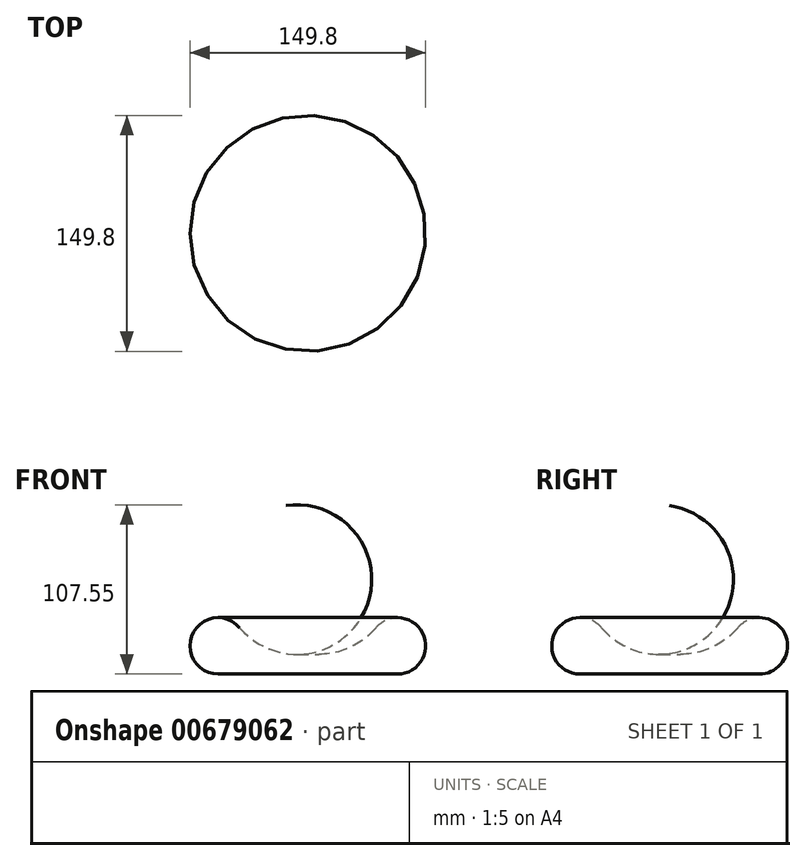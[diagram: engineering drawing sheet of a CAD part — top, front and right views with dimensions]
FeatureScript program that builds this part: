
annotation { "Feature Type Name" : "Feature", "Feature Type Description" : "" }
export const myFeature = defineFeature(function(context is Context, id is Id, definition is map)
    precondition{}
    {
        {
            var Q0;
            Q0=qCreatedBy(makeId("Right.planeOp"),FACE);
            var sketch = newSketch(context, id + "F0", { "sketchPlane" : qUnion([Q0])});
            skLineSegment(sketch, "E0", {"start": v(0, 0) * mm, "end": v(0, 13.09) * mm});
            skLineSegment(sketch, "E1", {"start": v(0, 0) * mm, "end": v(-56.98, 0) * mm});
            skArc(sketch, "E2", {"start": v(-43.28, 29.46) * mm, "mid": v(-73.22, 25.47) * mm, "end": v(-56.98, 0) * mm});
            skArc(sketch, "E3", {"start": v(-43.28, 29.46) * mm, "mid": v(-23.77, 15.65) * mm, "end": v(0, 13.09) * mm});
            skCircle(sketch, "E4", {"center": v(-56.98, 17.92) * mm, "radius": 13.02 * mm});
            skSolve(sketch);
        }
        {
            var Q0;
            Q0=makeQuery(id+"F0.imprint","IMPRINT",FACE,{"disambiguationData":[TD([[makeQuery(id+"F0.imprint","IMPRINT",EDGE,{"derivedFrom":sQuery(id+"F0.wireOp",EDGE,"E0")}),1.0]])]});
            var Q1;
            Q1=makeQuery(id+"F0.imprint","IMPRINT",FACE,{"disambiguationData":[TD([[makeQuery(id+"F0.imprint","IMPRINT",EDGE,{"derivedFrom":sQuery(id+"F0.wireOp",EDGE,"E4")}),1.0]])]});
            var Q2;
            Q2=sQuery(id+"F0.wireOp",EDGE,"E0");
            revolve(context, id + "F1", {"entities" : qUnion([Q0, Q1]), "axis" : qUnion([Q2]), "revolveType" : RevolveType.FULL});
        }
    });
